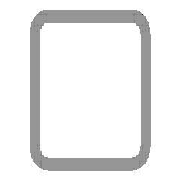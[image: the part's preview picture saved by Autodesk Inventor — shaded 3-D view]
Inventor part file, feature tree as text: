
AUTODESK INVENTOR PART (.ipt)
format: ipt  version: 2025.3 (Build 293356030, 356C)  size: 154,624 bytes
history: native  units: mm (DEFAULTED — no unit token found)
features: other x4, plane x3, split x2, sketch x1
ambient origin geometry x8: Origin, YZ Plane, XZ Plane, XY Plane, X Axis, Y Axis, Z Axis, Center Point
bodies: Solid1 (feature_tree), Body (feature_tree)
feature tree (10):
  parser-record x1  (decoder bookkeeping rows leaked as tree rows — omitted from the tree; the rows remain in map.json)
  other  "Driven Length"
  other  "Start Plane"
  other  "End Plane"
  plane  "Work Plane4"
  split  "Split1"
  plane  "Work Plane5"
  split  "Split2"
  sketch  "Sketch3"  dims[d3=2216.344931mm d4=0.0mm d7=6.0mm d9=80.0mm d11=80.0mm d12=3.0mm d13=-14.545455mm d14=2201.799476mm d15=40.0mm d16=40.0mm d17=90.0deg d18=2216.344931mm]
  plane  "Work Plane3"
